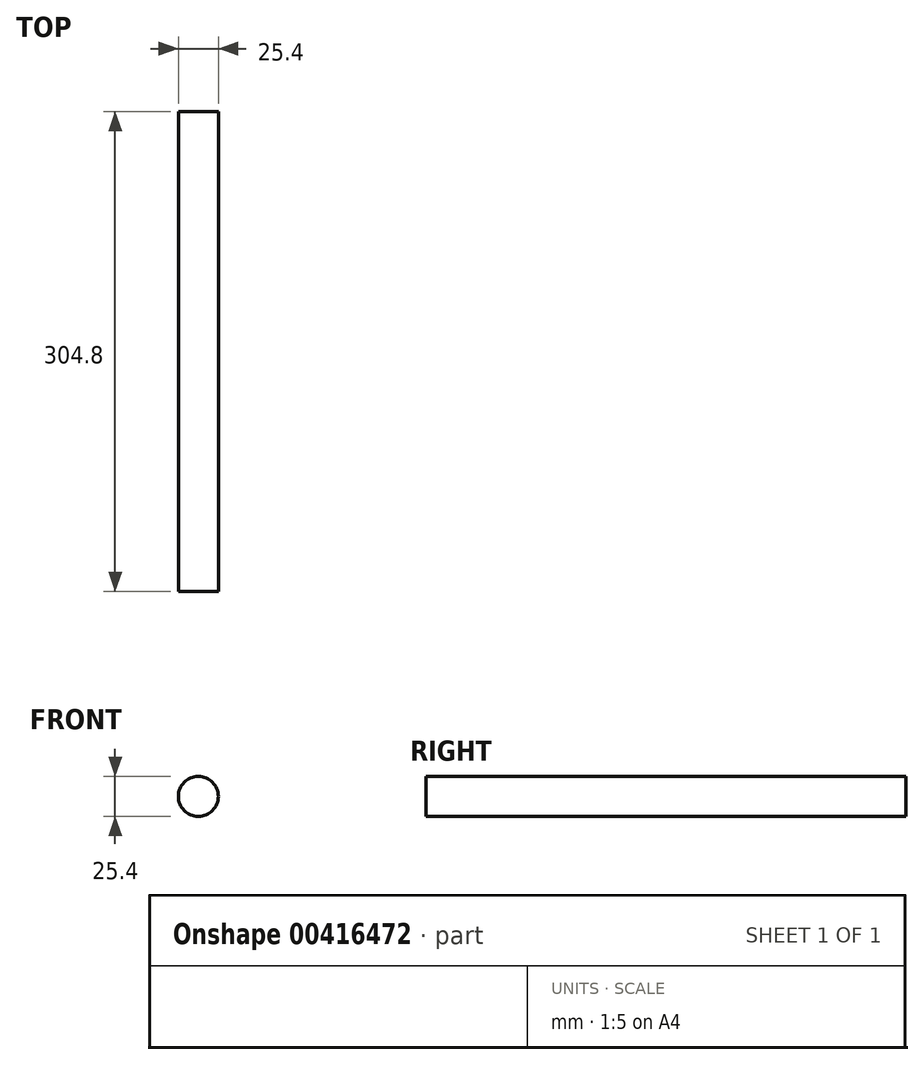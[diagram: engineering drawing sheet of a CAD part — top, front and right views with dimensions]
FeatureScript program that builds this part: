
annotation { "Feature Type Name" : "Feature", "Feature Type Description" : "" }
export const myFeature = defineFeature(function(context is Context, id is Id, definition is map)
    precondition{}
    {
        {
            var Q0;
            Q0=qCreatedBy(makeId("Front.planeOp"),FACE);
            var sketch = newSketch(context, id + "F0", { "sketchPlane" : qUnion([Q0])});
            skCircle(sketch, "E0", {"center": v(0, 0) * mm, "radius": 12.7 * mm});
            skSolve(sketch);
        }
        {
            var Q0;
            Q0 = qSketchRegion(id + "F0", true);
            extrude(context, id + "F1", {"entities" : qUnion([Q0]), "depth" : 304.8 * mm});
        }
    });
